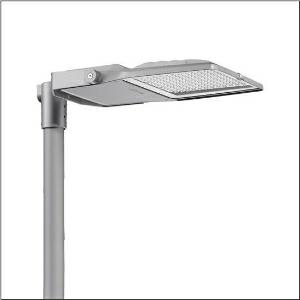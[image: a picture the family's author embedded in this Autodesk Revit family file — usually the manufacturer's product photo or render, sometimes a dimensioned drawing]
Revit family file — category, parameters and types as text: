
# Revit family: floodlight_fl_21_iq_midi___pl33t_5xa7781e4f3a_bb4e
name_source: partatom
category: Lighting Fixtures
units: mm (PartAtom-declared; Revit-internal decimal feet)

## family parameters
Cut with Voids When Loaded = No
Host = Face
Light Source = No
Part Type = Normal
Room Calculation Point = No
Round Connector Dimension = Use Diameter
Shared = No

## types (1)
- --- (1 x LED, 27690 lm, 208.1 W, 4000K)
    Apparent Load = 208 VA
    CIE Flux Codes = 26 75 99 100 100
    Color Rendering = 70
    Color Temperature = 4000K
    Default Elevation = 1800 mm
    Description = Floodlight FL 21 iQ midi, floodlight, primary light control with lens, of PMMA, primary optical cover: protective disc, of toughened safety glass, transparent, light distribution: PL33T, light emission: direct distribution, installation type: surface-mounted, lamps: LED, High Power LED, rated values: 27.690lm | 208,1W | 133,1lm/W (begin service life); end service life: 27.690lm | 227,1W; at 50% lumin. flux: 13.845lm | 90,3W | 153,3lm/W, colour temperature: 4000K, colour rendering: CRI > 70, light colour: 740, light setting 1 begin service life: 100% | 27.690lm | 208,1W | 133,1lm/W | 4.000K, light setting 1 end service life: 227,1W, further light settings possible, control: optimised constant luminous flux control (CLO 2.0), Desk-Remote (wireless, voltage-free reading and setting of iQ features in the workshop via application-optimized NFC function/RFID function), Light-Fading, Smart-Wire, Night-Set, Lumen-Switch, Temp-Guard, Auto-Match, pre-setting: linear dimming characteristic, with terminal, 6-pole, mains connection: 220..240V, AC, 50/60Hz, luminaire housing, of diecast aluminium, powder-coated, SITECO metallic grey (DB 702S), corrosivity category C5 mid according to DIN EN ISO 12944suitable for swimming poolschlorine-resistant, sealing non-destructively replaceable, please order mast flange separately, mast bracket, of steel, galvanised, powder-coated, SITECO metallic grey (DB 702S), protection rating (complete): IP66, insulation class (complete): insulation class II (safety insulation), certification: CE, ENEC, VDE, protection symbol: D, impact resistance: IK08, permissible operating ambient temperature: -40..+40°C, permissible operating ambient temperature for outdoor applications: -40..+50°C, standard: DIN EN 12944, LABS conformity tested according to VDMA 24364:2018-05, packaging unit: 1 piece

Light Distribution: PL33T
    Height = 76 mm
    Lamp = 1 x LED
    Lamp Light Flux = 27690 lm
    Lamp Power = 208.1 W
    Lamp count = 1
    Length = 657 mm
    Luminous efficacy = 133 lm/W
    Manufacturer = Siteco
    ModVariant = No
    Model = 5XA7781E4F3A
    Number of Poles = 1
    OnlyDefault = Yes
    Power Factor = 1
    Product Name = Floodlight FL 21 iQ midi | PL33T
    Product group = floodlight | pylon annexe
    ProductGroupID = 6201
    Protection Class = Protection class II
    Protection Degree = IP 66
    RLX_Detail_Level = 1
    RLX_Emergency_Light_Flux = 0 lm
    RLX_Emergency_Type = 0
    RLX_Emergency_Type_DB = No
    RlxData = <blob elided: 153805 chars, md5=138f0845>
    Socket = socket
    Standby Power = 0 W
    System Light Flux = 27690 lm
    System Power = 208 W
    Type Comments = factory setting: luminous flux: 100 % | dim-lin: 254 | 710 mA
    Type Image = l_1007123.jpg
    URL = http://relux.com
    VarID = @adj_103889
    Voltage = 0 V
    Weight = 0.00 kg
    Width = 442 mm

## geometry (parser evidence)
native form markers: Blend x4, Sweep x11
no freeform markers — native parametric forms only
